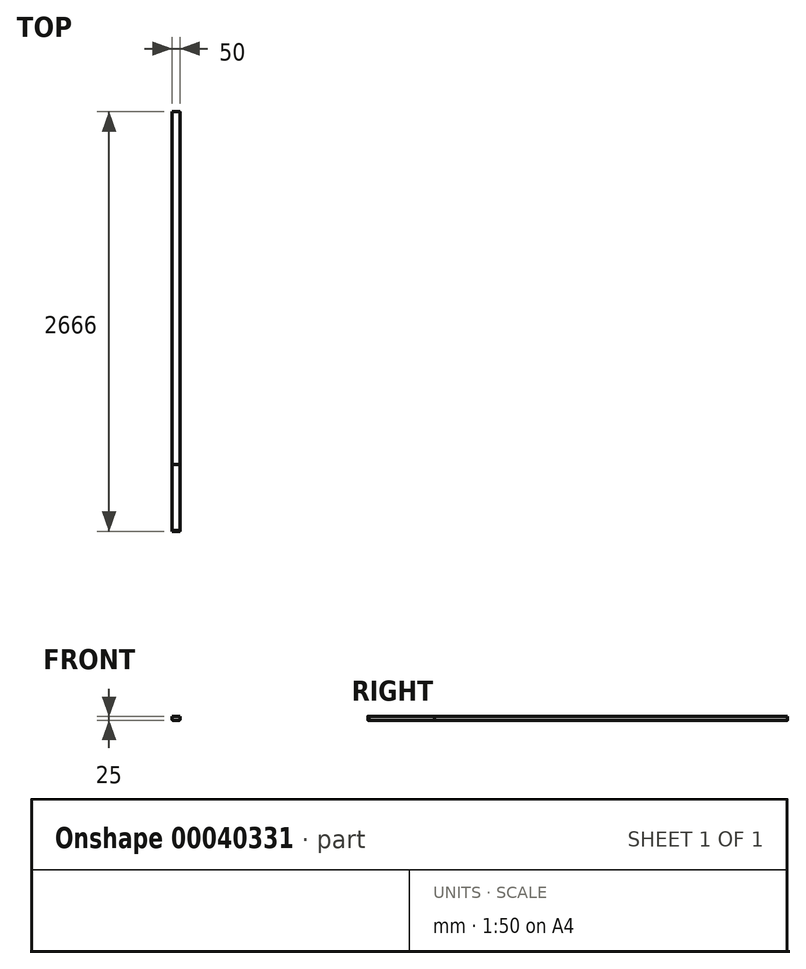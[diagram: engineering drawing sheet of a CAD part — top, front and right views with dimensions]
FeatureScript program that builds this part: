
annotation { "Feature Type Name" : "Feature", "Feature Type Description" : "" }
export const myFeature = defineFeature(function(context is Context, id is Id, definition is map)
    precondition{}
    {
        {
            var Q0;
            Q0=qCreatedBy(makeId("Front.planeOp"),FACE);
            var sketch = newSketch(context, id + "F0", { "sketchPlane" : qUnion([Q0])});
            skCircle(sketch, "E0", {"center": v(0, 0) * mm, "radius": 210 * mm, "construction": true});
            skLineSegment(sketch, "E1", {"start": v(0, 210) * mm, "end": v(0, -210) * mm});
            skArc(sketch, "E2", {"start": v(0, -210) * mm, "mid": v(210, 0) * mm, "end": v(0, 210) * mm});
            skSolve(sketch);
        }
        {
            var Q0;
            Q0=qCreatedBy(makeId("Front.planeOp"),FACE);
            cPlane(context, id + "F1", {"entities" : qUnion([Q0]), "cplaneType" : CPlaneType.OFFSET, "offset" : 461 * mm + 500 * mm + 162 * mm - 5 * mm, "oppositeDirection" : true, "width" : 152.4 * mm, "height" : 152.4 * mm});
        }
        {
            var Q0;
            Q0=qCreatedBy(id+"F1.planeOp",FACE);
            var sketch = newSketch(context, id + "F2", { "sketchPlane" : qUnion([Q0])});
            skLineSegment(sketch, "E3", {"start": v(25.68, -95.38) * mm, "end": v(-26.31, 97.74) * mm});
            skLineSegment(sketch, "E4", {"start": v(0, 0) * mm, "end": v(1006.86, 1.18) * mm, "construction": true});
            skPoint(sketch, "E4.endSnap0", {"position": v(-0.32, 1.18) * mm});
            skLineSegment(sketch, "E5", {"start": v(1261.18, 443.08) * mm, "end": v(1313.17, 249.96) * mm});
            skLineSegment(sketch, "E6", {"start": v(1287.17, 346.52) * mm, "end": v(0, 0) * mm, "construction": true});
            skLineSegment(sketch, "E7", {"start": v(1261.18, 443.08) * mm, "end": v(-26.31, 97.74) * mm});
            skLineSegment(sketch, "E8", {"start": v(1313.17, 249.96) * mm, "end": v(25.68, -95.38) * mm});
            skSolve(sketch);
        }
        {
            var Q0;
            Q0=makeQuery(id+"F0.imprint","IMPRINT",FACE,{"disambiguationData":[TD([[makeQuery(id+"F0.imprint","IMPRINT",EDGE,{"derivedFrom":sQuery(id+"F0.wireOp",EDGE,"E1")}),1.0]])]});
            var Q1;
            Q1=sQuery(id+"F0.wireOp",EDGE,"E1");
            revolve(context, id + "F3", {"entities" : qUnion([Q0]), "axis" : qUnion([Q1]), "revolveType" : RevolveType.FULL});
        }
        {
            var Q0;
            Q0=makeQuery(id+"F2.imprint","IMPRINT",FACE,{"disambiguationData":[TD([[makeQuery(id+"F2.imprint","IMPRINT",EDGE,{"derivedFrom":sQuery(id+"F2.wireOp",EDGE,"E3")}),-1.0]])]});
            var Q1;
            Q1=sQuery(id+"F2.wireOp",EDGE,"E3");
            revolve(context, id + "F4", {"entities" : qUnion([Q0]), "axis" : qUnion([Q1]), "revolveType" : RevolveType.FULL});
        }
        {
            var Q0;
            Q0=qCreatedBy(makeId("Front.planeOp"),FACE);
            var sketch = newSketch(context, id + "F5", { "sketchPlane" : qUnion([Q0])});
            skLineSegment(sketch, "E9.rect.bottom", {"start": v(25, 12.5) * mm, "end": v(-25, 12.5) * mm});
            skLineSegment(sketch, "E9.rect.top", {"start": v(25, -12.5) * mm, "end": v(-25, -12.5) * mm});
            skLineSegment(sketch, "E9.rect.left", {"start": v(25, 12.5) * mm, "end": v(25, -12.5) * mm});
            skLineSegment(sketch, "E9.rect.right", {"start": v(-25, 12.5) * mm, "end": v(-25, -12.5) * mm});
            skPoint(sketch, "E9.rect.middle", {"position": v(0, 0) * mm});
            skLineSegment(sketch, "E10.rect.bottom", {"start": v(1644.14, 1392.69) * mm, "end": v(-1644.14, 1392.69) * mm});
            skLineSegment(sketch, "E10.rect.top", {"start": v(1644.14, -1392.69) * mm, "end": v(-1644.14, -1392.69) * mm});
            skLineSegment(sketch, "E10.rect.left", {"start": v(1644.14, 1392.69) * mm, "end": v(1644.14, -1392.69) * mm});
            skLineSegment(sketch, "E10.rect.right", {"start": v(-1644.14, 1392.69) * mm, "end": v(-1644.14, -1392.69) * mm});
            skSolve(sketch);
        }
        {
            var Q0;
            Q0=makeQuery(id+"F3.opRevolve","SWEPT_BODY",BODY,{"disambiguationData":[OSD([sQuery(id+"F0.wireOp",EDGE,"E1"),sQuery(id+"F0.wireOp",EDGE,"E2")])]});
            var Q1;
            Q1=makeQuery(id+"F4.opRevolve","SWEPT_BODY",BODY,{"disambiguationData":[OSD([sQuery(id+"F2.wireOp",EDGE,"E3"),sQuery(id+"F2.wireOp",EDGE,"E5"),sQuery(id+"F2.wireOp",EDGE,"E7"),sQuery(id+"F2.wireOp",EDGE,"E8")])]});
            booleanBodies(context, id + "F6", {"operationType" : BooleanOperationType.SUBTRACTION, "tools" : qUnion([Q0]), "targets" : qUnion([Q1]), "keepTools" : true});
        }
        {
            var Q0;
            Q0 = qSketchRegion(id + "F5", true);
            extrude(context, id + "F7", {"entities" : qUnion([Q0]), "operationType" : NewBodyOperationType.REMOVE, "endBound" : BoundingType.THROUGH_ALL, "oppositeDirection" : true, "depth" : 25 * mm, "hasSecondDirection" : true, "secondDirectionBound" : SecondDirectionBoundingType.THROUGH_ALL, "secondDirectionOppositeDirection" : false, "secondDirectionDepth" : 25 * mm});
        }
        {
            var Q0;
            Q0=makeQuery(id+"F7.boolean.opBoolean","COPY",EDGE,{"disambiguationData":[OD(0.0)],"derivedFrom":makeQuery(id+"F7.opExtrude","SWEPT_EDGE",EDGE,{"disambiguationData":[OSD([sQuery(id+"F5.wireOp",EDGE,"E9.rect.top"),sQuery(id+"F5.wireOp",EDGE,"E9.rect.right")])]})});
            var Q1;
            Q1=makeQuery(id+"F7.boolean.opBoolean","COPY",EDGE,{"disambiguationData":[OD(0.0)],"derivedFrom":makeQuery(id+"F7.opExtrude","SWEPT_EDGE",EDGE,{"disambiguationData":[OSD([sQuery(id+"F5.wireOp",EDGE,"E9.rect.top"),sQuery(id+"F5.wireOp",EDGE,"E9.rect.left")])]})});
            fillet(context, id + "F8", {"entities" : qUnion([Q0, Q1]), "radius" : 5 * mm, "tangentPropagation" : true, "allowEdgeOverflow" : false});
        }
    });
